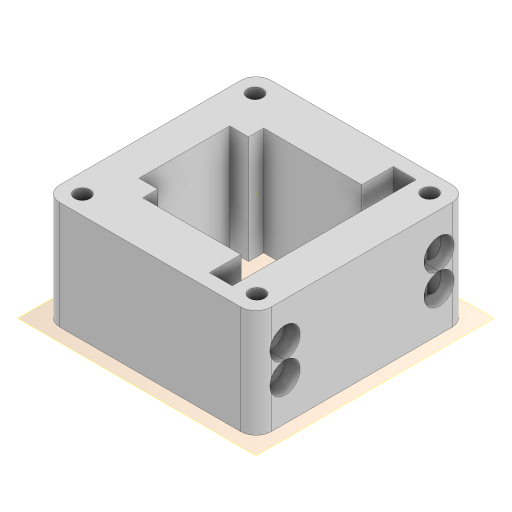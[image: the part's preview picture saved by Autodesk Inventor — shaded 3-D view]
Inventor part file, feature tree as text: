
AUTODESK INVENTOR PART (.ipt)
format: ipt  version: 2024.1 (Build 281209000, 209)  size: 242,688 bytes
history: native  units: mm
features: sketch x4, other x3, plane x2, extrude x2, reference x2, hole x1
ambient origin geometry x8: Origin, YZ Plane, XZ Plane, XY Plane, X Axis, Y Axis, Z Axis, Center Point
bodies: Volumenkörper1 (feature_tree)
feature tree (14):
  plane  "Arbeitsebene1"
  sketch  "Skizze1"  dims[d0=28.0mm d1=28.0mm]
  plane  "Arbeitsebene2"
  extrude  "Extrusion1"  Depth=28.0mm
  extrude  "Extrusion2"  Depth=10.0mm
  hole  "Bohrung1"  [1 undecoded]
  sketch  "Skizze4"  dims[d12=1.8mm d13=6.0mm d14=4.0mm d15=2.0mm d16=90.0deg d17=8.0mm d18=20.594885mm d19=16.0mm d20=16.0mm d21=3.0mm d22=9.0mm d23=9.0mm d24=5.0mm d25=12.0mm]
  reference  "Referenz1"
  sketch  "Skizze2"  dims[d2=2.0mm d3=10.0mm]
  sketch  "Skizze3"  dims[d4=10.0mm d5=0.0mm d10=10.0mm d11=0.0mm]
  reference  "Referenz6"
  other  "Assembly_Planktoscope_Uc2version_wormdrive_V3.iam"
  other  "60_Planktoscope_Base_half_wormdrive_1:1"
  other  "00_Micro_Stepper_15mm_Gearbox:1"
note: 1 required parameter value undecoded (feature->parameter linkage not recoverable at this tier; creation-order binding heuristic only, values carry confidence <= 0.55)
